# Revit family: DS
name_source: partatom
category: Air Terminals
revit_build: Autodesk Revit MEP 2012 (Build: 20110309_2315(x64)
units: mm (PartAtom-declared; Revit-internal decimal feet)

## types (6) — shared parameters
Manufacturer = INNES
Material = Aluminio
Máxima velocidad de chorro = 4000 FPM
Mínima velocidad de chorro = 750 FPM
URL = http://www.innes.com
ancho cinta A = 2"

## per-type parameters (varying)
| type | B | C | C int | D | E | G | Max Flow | Min Flow | Máxima presión estática | Máximo nivel de ruido (NC) | Mínima presión estática | a | ancho cinta B | b | c | g |
| DS-06 | 7 19/32" | 6" | 2 15/16" | 1 1/2" | 3 11/16" | 2 15/16" | 190 CFM | 40 CFM | 1.20 in-wg | 34 | 0.05 in-wg | 3 1/8" | 1/8" | 3 51/64" | 3" | 1 15/32" |
| DS-08 | 9 13/16" | 7 31/32" | 3 59/64" | 1 3/4" | 4 11/16" | 3 15/16" | 340 CFM | 60 CFM | 1.20 in-wg | 40 | 0.04 in-wg | 4 7/64" | 1/4" | 4 29/32" | 3 63/64" | 1 31/32" |
| DS-10 | 12 23/32" | 10 19/32" | 5 15/64" | 2 1/16" | 6 23/32" | 5 1/2" | 660 CFM | 120 CFM | 1.20 in-wg | 39 | 0.04 in-wg | 5 27/64" | 1/4" | 6 23/64" | 5 19/64" | 2 3/4" |
| DS-12 | 14 3/16" | 12 1/16" | 5 31/32" | 2 7/16" | 7 7/8" | 6 1/2" | 920 CFM | 170 CFM | 1.20 in-wg | 40 | 0.04 in-wg | 6 5/32" | 1/4" | 7 3/32" | 6 1/32" | 3 1/4" |
| DS-16 | 18 3/4" | 16 1/4" | 8 1/16" | 4 11/32" | 9 17/32" | 9 1/32" | 1790 CFM | 340 CFM | 1.19 in-wg | 45 | 0.04 in-wg | 8 1/4" | 1/4" | 9 3/8" | 8 1/8" | 4 33/64" |
| DS-20 | 21 1/16" | 18 19/32" | 9 15/64" | 3 25/32" | 11 17/32" | 12 7/32" | 3260 CFM | 610 CFM | 1.20 in-wg | 46 | 0.04 in-wg | 9 27/64" | 1/4" | 10 17/32" | 9 19/64" | 6 7/64" |

## geometry (parser evidence)
native form markers: Sweep x1
no freeform markers — native parametric forms only
